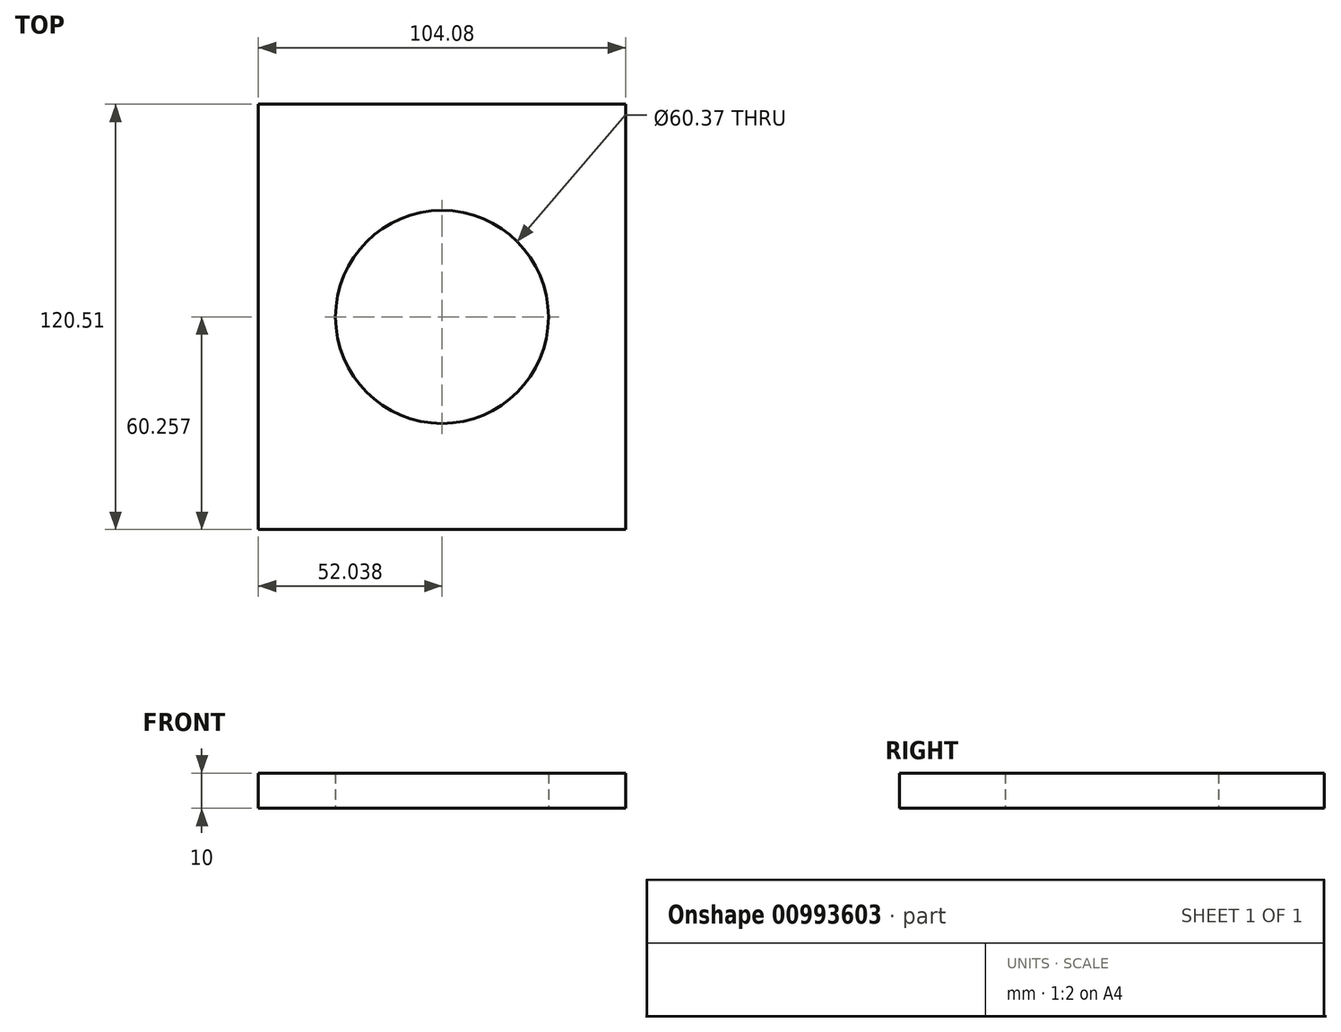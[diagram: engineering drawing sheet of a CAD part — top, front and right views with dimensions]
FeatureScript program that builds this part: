
annotation { "Feature Type Name" : "Feature", "Feature Type Description" : "" }
export const myFeature = defineFeature(function(context is Context, id is Id, definition is map)
    precondition{}
    {
        {
            var Q0;
            Q0=qCreatedBy(makeId("Top.planeOp"),FACE);
            var sketch = newSketch(context, id + "F0", { "sketchPlane" : qUnion([Q0])});
            skLineSegment(sketch, "E0", {"start": v(0, 0) * mm, "end": v(0, 120.51) * mm});
            skLineSegment(sketch, "E1", {"start": v(0, 120.51) * mm, "end": v(104.08, 120.51) * mm});
            skLineSegment(sketch, "E2", {"start": v(104.08, 120.51) * mm, "end": v(104.08, 0) * mm});
            skLineSegment(sketch, "E3", {"start": v(104.08, 0) * mm, "end": v(0, 0) * mm});
            skLineSegment(sketch, "E4", {"start": v(0, 120.51) * mm, "end": v(104.08, 0) * mm});
            skLineSegment(sketch, "E5", {"start": v(104.08, 120.51) * mm, "end": v(0, 0) * mm});
            skCircle(sketch, "E6", {"center": v(52.04, 60.26) * mm, "radius": 30.18 * mm});
            skSolve(sketch);
        }
        {
            var Q0;
            {var subQ0=sQuery(id+"F0.wireOp",EDGE,"E0");Q0=makeQuery(id+"F0.imprint","IMPRINT",FACE,{"disambiguationData":[TD([[makeQuery(id+"F0.imprint","IMPRINT",EDGE,{"derivedFrom":subQ0}),-1.0]])]});}
            var Q1;
            {var subQ0=sQuery(id+"F0.wireOp",EDGE,"E1");Q1=makeQuery(id+"F0.imprint","IMPRINT",FACE,{"disambiguationData":[TD([[makeQuery(id+"F0.imprint","IMPRINT",EDGE,{"derivedFrom":subQ0}),-1.0]])]});}
            var Q2;
            {var subQ0=sQuery(id+"F0.wireOp",EDGE,"E2");Q2=makeQuery(id+"F0.imprint","IMPRINT",FACE,{"disambiguationData":[TD([[makeQuery(id+"F0.imprint","IMPRINT",EDGE,{"derivedFrom":subQ0}),-1.0]])]});}
            var Q3;
            {var subQ0=sQuery(id+"F0.wireOp",EDGE,"E3");Q3=makeQuery(id+"F0.imprint","IMPRINT",FACE,{"disambiguationData":[TD([[makeQuery(id+"F0.imprint","IMPRINT",EDGE,{"derivedFrom":subQ0}),-1.0]])]});}
            extrude(context, id + "F1", {"entities" : qUnion([Q0, Q1, Q2, Q3]), "depth" : 10 * mm, "offsetDistance" : 25.4 * mm});
        }
    });
